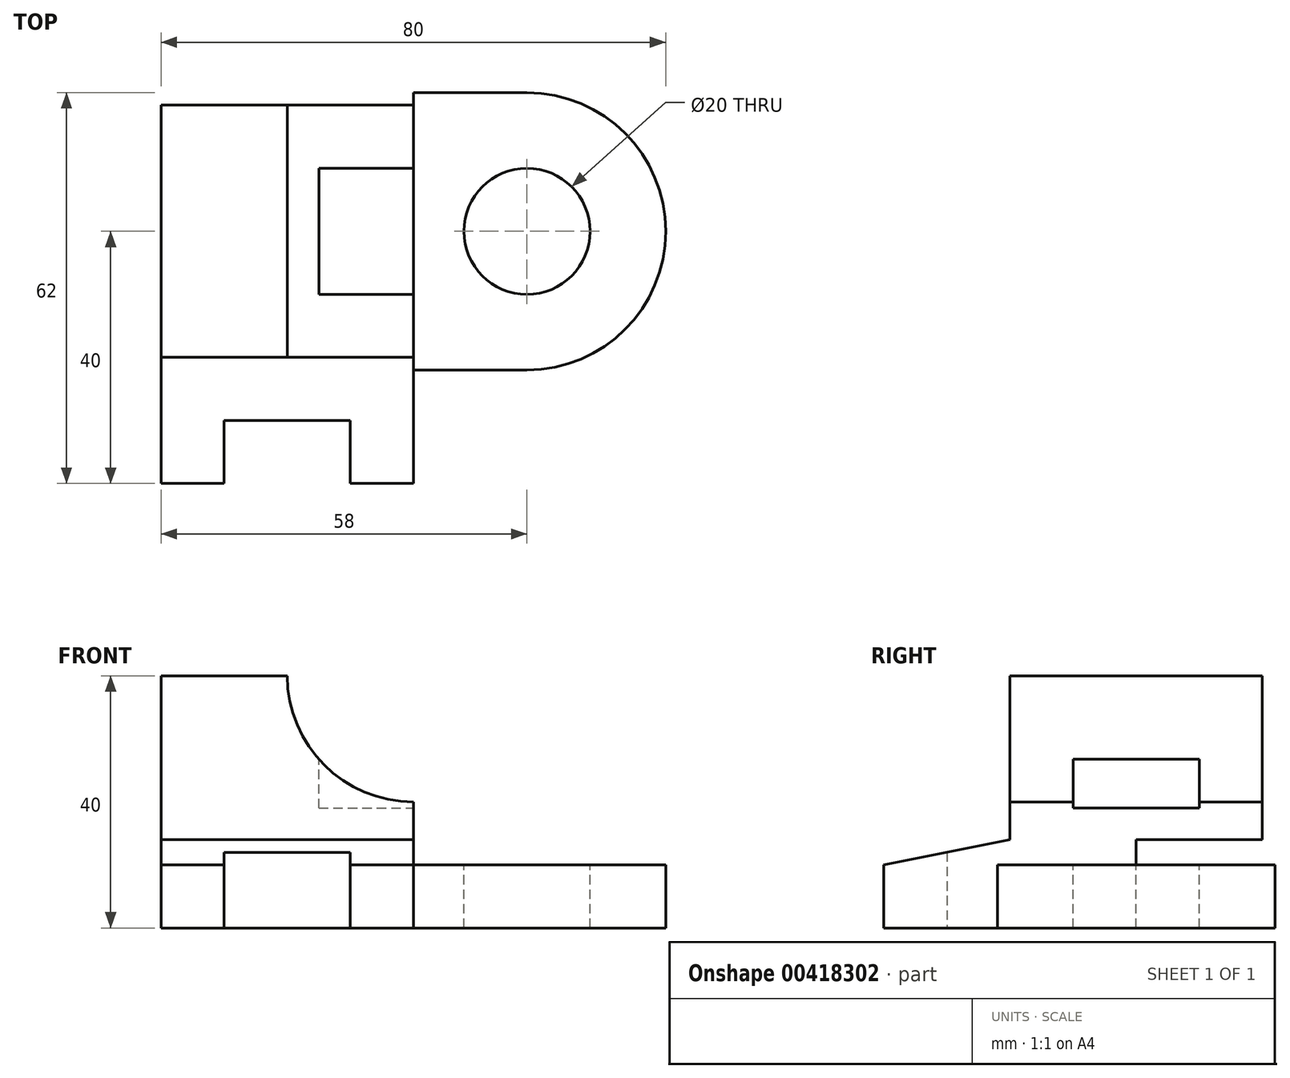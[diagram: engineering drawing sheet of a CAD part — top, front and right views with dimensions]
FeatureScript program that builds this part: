
annotation { "Feature Type Name" : "Feature", "Feature Type Description" : "" }
export const myFeature = defineFeature(function(context is Context, id is Id, definition is map)
    precondition{}
    {
        {
            var Q0;
            Q0=qCreatedBy(makeId("Front.planeOp"),FACE);
            var sketch = newSketch(context, id + "F0", { "sketchPlane" : qUnion([Q0])});
            skLineSegment(sketch, "E0", {"start": v(0, 0) * mm, "end": v(-40, 0) * mm});
            skLineSegment(sketch, "E1", {"start": v(-40, 0) * mm, "end": v(-40, 26) * mm});
            skLineSegment(sketch, "E2", {"start": v(-40, 26) * mm, "end": v(-20, 26) * mm});
            skLineSegment(sketch, "E3", {"start": v(-20, 26) * mm, "end": v(0, 26) * mm, "construction": true});
            skArc(sketch, "E4", {"start": v(-20, 26) * mm, "mid": v(-14.14, 11.86) * mm, "end": v(0, 6) * mm});
            skLineSegment(sketch, "E5", {"start": v(0, 0) * mm, "end": v(0, 6) * mm});
            skSolve(sketch);
        }
        {
            var Q0;
            Q0 = qSketchRegion(id + "F0", true);
            extrude(context, id + "F1", {"entities" : qUnion([Q0]), "endBound" : BoundingType.SYMMETRIC, "depth" : 40 * mm});
        }
        {
            var Q0;
            Q0=makeQuery(id+"F1.opExtrude","SWEPT_FACE",FACE,{"disambiguationData":[OSD([sQuery(id+"F0.wireOp",EDGE,"E0")])]});
            var sketch = newSketch(context, id + "F2", { "sketchPlane" : qUnion([Q0])});
            skLineSegment(sketch, "E6.bottom", {"start": v(-40, 0) * mm, "end": v(0, 0) * mm});
            skLineSegment(sketch, "E6.top", {"start": v(-40, 40) * mm, "end": v(0, 40) * mm});
            skLineSegment(sketch, "E6.left", {"start": v(-40, 0) * mm, "end": v(-40, 40) * mm});
            skLineSegment(sketch, "E6.right", {"start": v(0, 0) * mm, "end": v(0, 40) * mm});
            skSolve(sketch);
        }
        {
            var Q0;
            Q0 = qSketchRegion(id + "F2", true);
            extrude(context, id + "F3", {"entities" : qUnion([Q0]), "operationType" : NewBodyOperationType.ADD, "depth" : 14 * mm});
        }
        {
            var Q0;
            Q0=makeQuery(id+"F3.opExtrude","CAP_EDGE",EDGE,{"disambiguationData":[OSD([sQuery(id+"F2.wireOp",EDGE,"E6.top")])],"isStart":true});
            chamfer(context, id + "F4", {"entities" : qUnion([Q0]), "chamferType" : ChamferType.TWO_OFFSETS, "width1" : 20 * mm, "oppositeDirection" : false, "width2" : 4 * mm, "tangentPropagation" : true});
        }
        {
            var Q0;
            Q0=makeQuery(id+"F3.opExtrude","CAP_FACE",FACE,{"disambiguationData":[OSD([sQuery(id+"F2.wireOp",EDGE,"E6.bottom"),sQuery(id+"F2.wireOp",EDGE,"E6.top"),sQuery(id+"F2.wireOp",EDGE,"E6.left"),sQuery(id+"F2.wireOp",EDGE,"E6.right")])],"isStart":false});
            var sketch = newSketch(context, id + "F5", { "sketchPlane" : qUnion([Q0])});
            skLineSegment(sketch, "E7.bottom", {"start": v(-30, 40) * mm, "end": v(-10, 40) * mm});
            skLineSegment(sketch, "E7.top", {"start": v(-30, 30) * mm, "end": v(-10, 30) * mm});
            skLineSegment(sketch, "E7.left", {"start": v(-30, 40) * mm, "end": v(-30, 30) * mm});
            skLineSegment(sketch, "E7.right", {"start": v(-10, 40) * mm, "end": v(-10, 30) * mm});
            skSolve(sketch);
        }
        {
            var Q0;
            Q0 = qSketchRegion(id + "F5", true);
            extrude(context, id + "F6", {"entities" : qUnion([Q0]), "operationType" : NewBodyOperationType.REMOVE, "endBound" : BoundingType.THROUGH_ALL, "oppositeDirection" : true, "depth" : 25 * mm});
        }
        {
            var Q0;
            {var subQ0=sQuery(id+"F2.wireOp",EDGE,"E6.right");var subQ1=sQuery(id+"F2.wireOp",EDGE,"E6.left");var subQ2=sQuery(id+"F2.wireOp",EDGE,"E6.top");var subQ3=sQuery(id+"F2.wireOp",EDGE,"E6.bottom");Q0=makeQuery(id+"FMFLvO2zIKUCswZ_1.1.F3.boolean.opBoolean","MERGE",FACE,{"derivedFrom":[makeQuery(id+"F3.opExtrude","CAP_FACE",FACE,{"disambiguationData":[OSD([subQ3,subQ2,subQ1,subQ0])],"isStart":false}),makeQuery(id+"FMFLvO2zIKUCswZ_1.1.F3.opExtrude","CAP_FACE",FACE,{"disambiguationData":[OSD([subQ3,subQ2,subQ1,subQ0])],"isStart":false})]});}
            var sketch = newSketch(context, id + "F7", { "sketchPlane" : qUnion([Q0])});
            skLineSegment(sketch, "E8.bottom", {"start": v(0, 22) * mm, "end": v(40, 22) * mm});
            skLineSegment(sketch, "E8.top", {"start": v(0, -22) * mm, "end": v(40, -22) * mm});
            skLineSegment(sketch, "E8.left", {"start": v(0, 22) * mm, "end": v(0, -22) * mm});
            skLineSegment(sketch, "E8.right", {"start": v(40, 22) * mm, "end": v(40, -22) * mm});
            skSolve(sketch);
        }
        {
            var Q0;
            Q0 = qSketchRegion(id + "F7", true);
            extrude(context, id + "F8", {"entities" : qUnion([Q0]), "operationType" : NewBodyOperationType.ADD, "oppositeDirection" : true, "depth" : 10 * mm});
        }
        {
            var Q0;
            Q0=makeQuery(id+"F8.opExtrude","SWEPT_EDGE",EDGE,{"disambiguationData":[OSD([sQuery(id+"F7.wireOp",EDGE,"E8.bottom"),sQuery(id+"F7.wireOp",EDGE,"E8.right")])]});
            var Q1;
            Q1=makeQuery(id+"F8.opExtrude","SWEPT_EDGE",EDGE,{"disambiguationData":[OSD([sQuery(id+"F7.wireOp",EDGE,"E8.top"),sQuery(id+"F7.wireOp",EDGE,"E8.right")])]});
            fillet(context, id + "F9", {"entities" : qUnion([Q0, Q1]), "radius" : 22 * mm, "tangentPropagation" : true, "allowEdgeOverflow" : false});
        }
        {
            var Q0;
            Q0=makeQuery(id+"F8.opExtrude","CAP_FACE",FACE,{"disambiguationData":[OSD([sQuery(id+"F7.wireOp",EDGE,"E8.bottom"),sQuery(id+"F7.wireOp",EDGE,"E8.top"),sQuery(id+"F7.wireOp",EDGE,"E8.left"),sQuery(id+"F7.wireOp",EDGE,"E8.right")])],"isStart":false});
            var sketch = newSketch(context, id + "F10", { "sketchPlane" : qUnion([Q0])});
            skCircle(sketch, "E9", {"center": v(18, 0) * mm, "radius": 10 * mm});
            skSolve(sketch);
        }
        {
            var Q0;
            Q0 = qSketchRegion(id + "F10", true);
            extrude(context, id + "F11", {"entities" : qUnion([Q0]), "operationType" : NewBodyOperationType.REMOVE, "endBound" : BoundingType.THROUGH_ALL, "oppositeDirection" : true, "depth" : 25 * mm});
        }
        {
            var Q0;
            Q0=makeQuery(id+"F1.opExtrude","SWEPT_FACE",FACE,{"disambiguationData":[OSD([sQuery(id+"F0.wireOp",EDGE,"E2")])]});
            var sketch = newSketch(context, id + "F12", { "sketchPlane" : qUnion([Q0])});
            skLineSegment(sketch, "E10.bottom", {"start": v(-15, 10) * mm, "end": v(0, 10) * mm});
            skLineSegment(sketch, "E10.top", {"start": v(-15, -10) * mm, "end": v(0, -10) * mm});
            skLineSegment(sketch, "E10.left", {"start": v(-15, 10) * mm, "end": v(-15, -10) * mm});
            skLineSegment(sketch, "E10.right", {"start": v(0, 10) * mm, "end": v(0, -10) * mm});
            skSolve(sketch);
        }
        {
            var Q0;
            Q0 = qSketchRegion(id + "F12", true);
            extrude(context, id + "F13", {"entities" : qUnion([Q0]), "operationType" : NewBodyOperationType.REMOVE, "oppositeDirection" : true, "depth" : 21 * mm});
        }
    });
